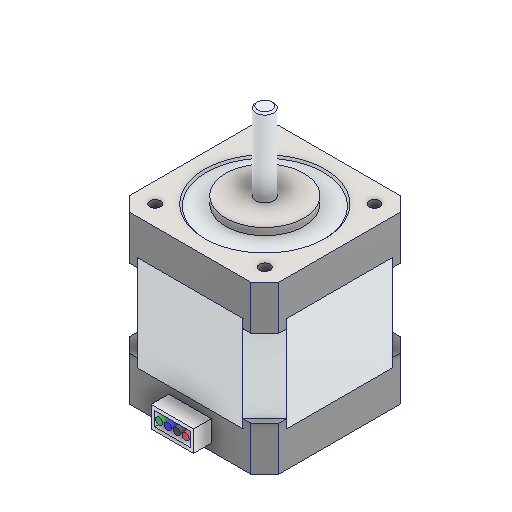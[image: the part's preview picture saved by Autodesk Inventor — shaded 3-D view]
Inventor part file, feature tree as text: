
AUTODESK INVENTOR PART (.ipt)
format: ipt  version: 2022 (Build 260153000, 153)  size: 200,192 bytes
history: native  units: mm
features: other x8, chamfer x2
ambient origin geometry x8: Origin, YZ Plane, XZ Plane, XY Plane, X Axis, Y Axis, Z Axis, Center Point
bodies: Body1 (feature_tree), Body2 (feature_tree), Body3 (feature_tree), Body4 (feature_tree), Body5 (feature_tree)
feature tree (10):
  other  "Твердое тело1"
  other  "Твердое тело2"
  other  "Твердое тело3"
  other  "Твердое тело4"
  other  "Твердое тело5"
  other  "Boss-Extrude8"
  other  "Boss-Extrude9"
  chamfer  "Chamfer1"  [1 undecoded]
  chamfer  "Chamfer2"  [1 undecoded]
  other  "Boss-Extrude12"
note: 2 required parameter values undecoded (feature->parameter linkage not recoverable at this tier; creation-order binding heuristic only, values carry confidence <= 0.55)
